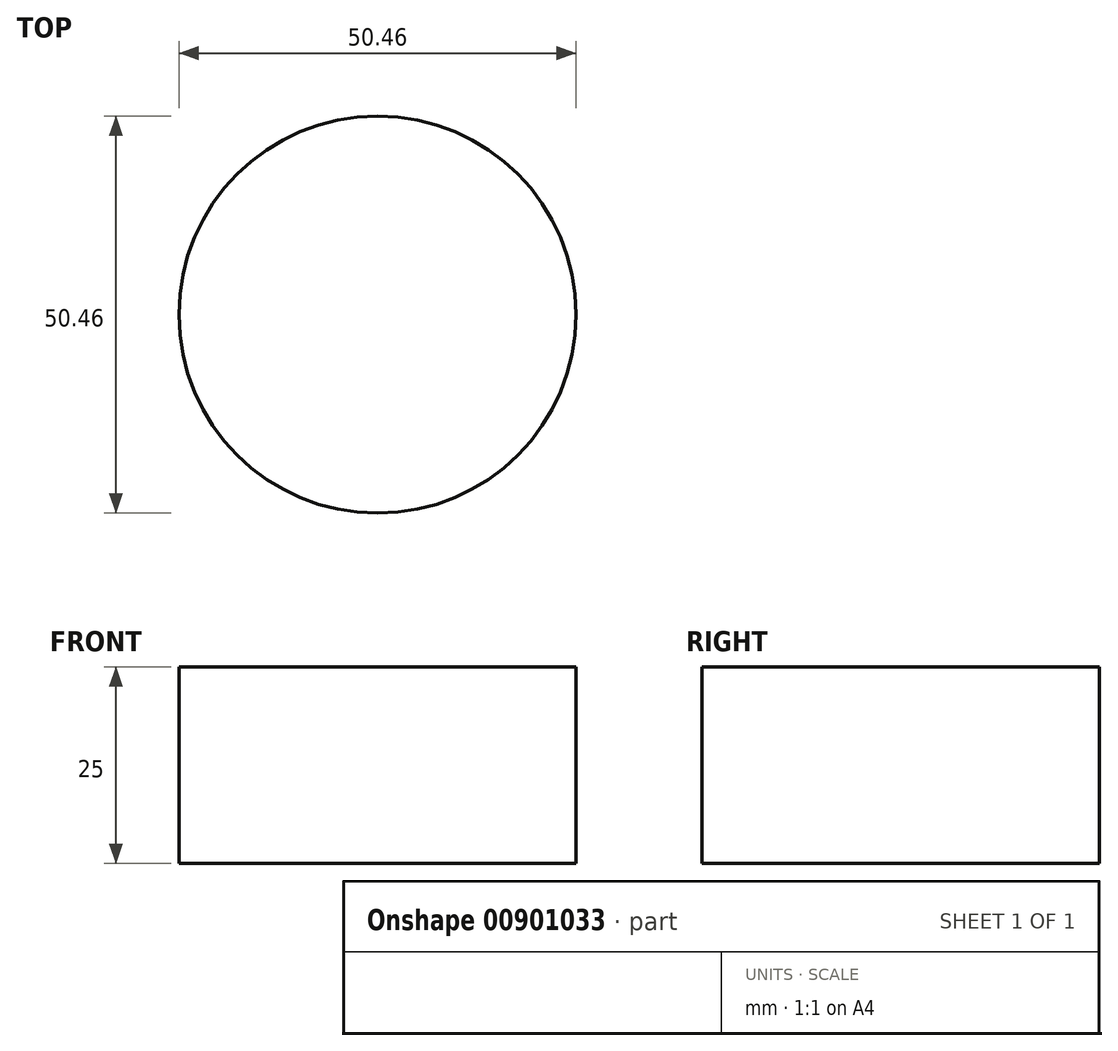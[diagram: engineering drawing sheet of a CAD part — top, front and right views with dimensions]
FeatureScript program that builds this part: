
annotation { "Feature Type Name" : "Feature", "Feature Type Description" : "" }
export const myFeature = defineFeature(function(context is Context, id is Id, definition is map)
    precondition{}
    {
        {
            var Q0;
            Q0=qCreatedBy(makeId("Top.planeOp"),FACE);
            var sketch = newSketch(context, id + "F0", { "sketchPlane" : qUnion([Q0])});
            skCircle(sketch, "E0", {"center": v(0, 0) * mm, "radius": 25.23 * mm});
            skSolve(sketch);
        }
        {
            var Q0;
            Q0 = qSketchRegion(id + "F0", true);
            extrude(context, id + "F1", {"entities" : qUnion([Q0]), "depth" : 25 * mm, "offsetDistance" : 25 * mm});
        }
    });
